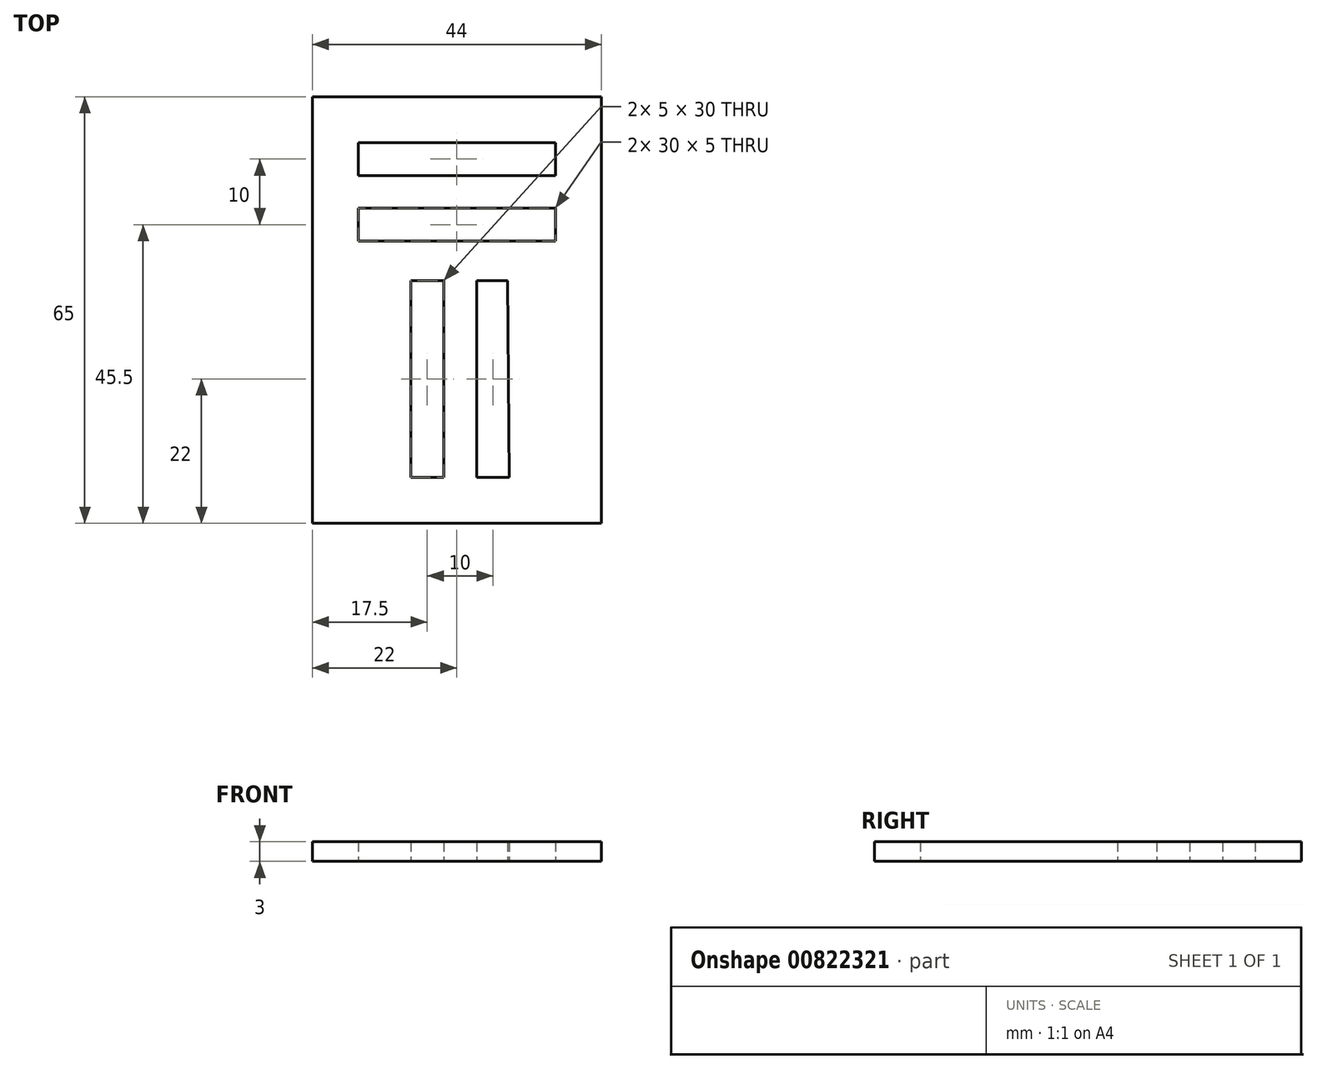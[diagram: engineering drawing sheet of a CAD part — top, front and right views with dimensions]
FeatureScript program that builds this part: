
annotation { "Feature Type Name" : "Feature", "Feature Type Description" : "" }
export const myFeature = defineFeature(function(context is Context, id is Id, definition is map)
    precondition{}
    {
        {
            var Q0;
            Q0=qCreatedBy(makeId("Top.planeOp"),FACE);
            var sketch = newSketch(context, id + "F0", { "sketchPlane" : qUnion([Q0])});
            skLineSegment(sketch, "E0.bottom", {"start": v(22, -32.5) * mm, "end": v(-22, -32.5) * mm});
            skLineSegment(sketch, "E0.top", {"start": v(22, 32.5) * mm, "end": v(-22, 32.5) * mm});
            skLineSegment(sketch, "E0.left", {"start": v(22, -32.5) * mm, "end": v(22, 32.5) * mm});
            skLineSegment(sketch, "E0.right", {"start": v(-22, -32.5) * mm, "end": v(-22, 32.5) * mm});
            skPoint(sketch, "E0.middle", {"position": v(0, 0) * mm});
            skLineSegment(sketch, "E1", {"start": v(-22, -32.5) * mm, "end": v(-7, -32.5) * mm});
            skLineSegment(sketch, "E2", {"start": v(-7, -32.5) * mm, "end": v(-7, -25.5) * mm});
            skLineSegment(sketch, "E3", {"start": v(-7, -25.5) * mm, "end": v(-2, -25.5) * mm});
            skLineSegment(sketch, "E4", {"start": v(-2, -25.5) * mm, "end": v(-2, 4.5) * mm});
            skLineSegment(sketch, "E5", {"start": v(-2, 4.5) * mm, "end": v(-7, 4.5) * mm});
            skLineSegment(sketch, "E6", {"start": v(-7, 4.5) * mm, "end": v(-7, -25.5) * mm});
            skLineSegment(sketch, "E7", {"start": v(8, -25.5) * mm, "end": v(3, -25.5) * mm});
            skLineSegment(sketch, "E8", {"start": v(3, -25.5) * mm, "end": v(3, 4.5) * mm});
            skLineSegment(sketch, "E9", {"start": v(3, 4.5) * mm, "end": v(7.7, 4.5) * mm});
            skLineSegment(sketch, "E10", {"start": v(7.7, 4.5) * mm, "end": v(8, -25.5) * mm});
            skLineSegment(sketch, "E11", {"start": v(-22, 32.5) * mm, "end": v(-22, 25.5) * mm});
            skLineSegment(sketch, "E12", {"start": v(-22, 25.5) * mm, "end": v(-15, 25.5) * mm});
            skLineSegment(sketch, "E13", {"start": v(-15, 25.5) * mm, "end": v(-15, 20.5) * mm});
            skLineSegment(sketch, "E14", {"start": v(-15, 20.5) * mm, "end": v(15, 20.5) * mm});
            skLineSegment(sketch, "E15", {"start": v(15, 20.5) * mm, "end": v(15, 25.5) * mm});
            skLineSegment(sketch, "E16", {"start": v(15, 25.5) * mm, "end": v(-15, 25.5) * mm});
            skLineSegment(sketch, "E17", {"start": v(-15, 20.5) * mm, "end": v(-15, 15.5) * mm});
            skLineSegment(sketch, "E18", {"start": v(-15, 15.5) * mm, "end": v(15, 15.5) * mm});
            skLineSegment(sketch, "E19", {"start": v(15, 15.5) * mm, "end": v(15, 10.5) * mm});
            skLineSegment(sketch, "E20", {"start": v(15, 10.5) * mm, "end": v(-15, 10.5) * mm});
            skLineSegment(sketch, "E21", {"start": v(-15, 10.5) * mm, "end": v(-15, 15.5) * mm});
            skLineSegment(sketch, "E22", {"start": v(-2, -25.5) * mm, "end": v(3, -25.5) * mm});
            skSolve(sketch);
        }
        {
            var Q0;
            Q0=makeQuery(id+"F0.imprint","IMPRINT",FACE,{"disambiguationData":[TD([[makeQuery(id+"F0.imprint","IMPRINT",EDGE,{"derivedFrom":sQuery(id+"F0.wireOp",EDGE,"E0.bottom")}),-1.0]])]});
            extrude(context, id + "F1", {"entities" : qUnion([Q0]), "depth" : 3 * mm, "offsetDistance" : 25.4 * mm});
        }
    });
